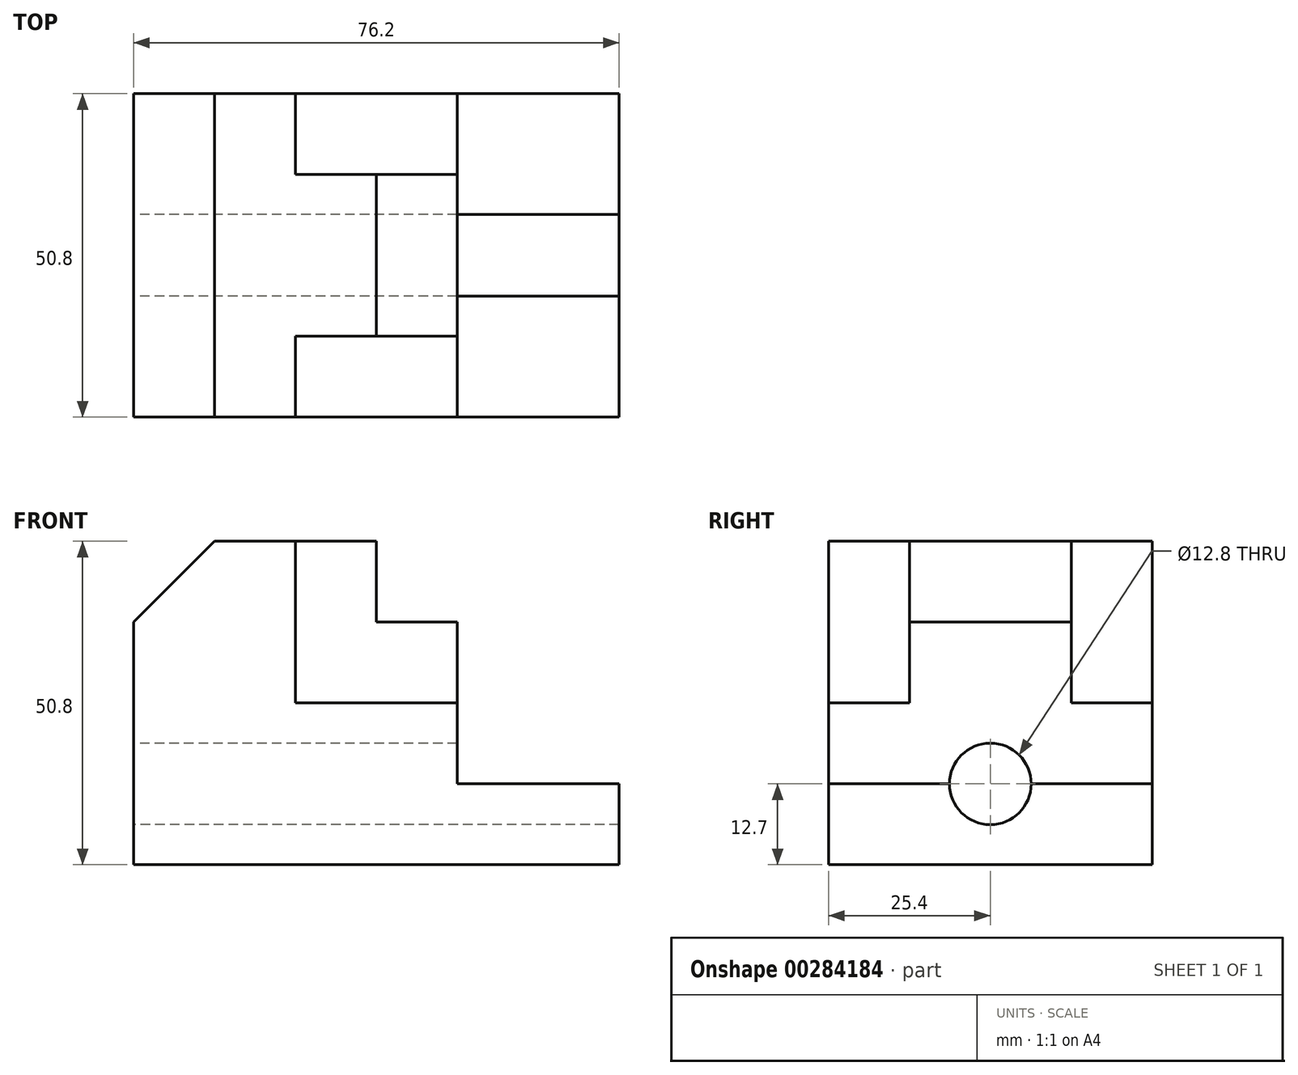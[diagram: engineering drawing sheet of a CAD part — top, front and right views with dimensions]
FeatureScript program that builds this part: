
annotation { "Feature Type Name" : "Feature", "Feature Type Description" : "" }
export const myFeature = defineFeature(function(context is Context, id is Id, definition is map)
    precondition{}
    {
        {
            var Q0;
            Q0=qCreatedBy(makeId("Front.planeOp"),FACE);
            var sketch = newSketch(context, id + "F0", { "sketchPlane" : qUnion([Q0])});
            skLineSegment(sketch, "E0", {"start": v(0, 0) * mm, "end": v(76.2, 0) * mm});
            skLineSegment(sketch, "E1", {"start": v(76.2, 0) * mm, "end": v(76.2, 12.7) * mm});
            skLineSegment(sketch, "E2", {"start": v(76.2, 12.7) * mm, "end": v(50.8, 12.7) * mm});
            skLineSegment(sketch, "E3", {"start": v(50.8, 12.7) * mm, "end": v(50.8, 38.1) * mm});
            skLineSegment(sketch, "E4", {"start": v(50.8, 38.1) * mm, "end": v(38.1, 38.1) * mm});
            skLineSegment(sketch, "E5", {"start": v(38.1, 38.1) * mm, "end": v(38.1, 50.8) * mm});
            skLineSegment(sketch, "E6", {"start": v(38.1, 50.8) * mm, "end": v(12.7, 50.8) * mm});
            skLineSegment(sketch, "E7", {"start": v(12.7, 50.8) * mm, "end": v(0, 38.1) * mm});
            skLineSegment(sketch, "E8", {"start": v(0, 38.1) * mm, "end": v(0, 0) * mm});
            skSolve(sketch);
        }
        {
            var Q0;
            Q0=makeQuery(id+"F0.imprint","IMPRINT",FACE,{"disambiguationData":[TD([[makeQuery(id+"F0.imprint","IMPRINT",EDGE,{"derivedFrom":sQuery(id+"F0.wireOp",EDGE,"E0")}),1.0]])]});
            extrude(context, id + "F1", {"entities" : qUnion([Q0]), "depth" : 50.8 * mm, "symmetric" : true});
        }
        {
            var Q0;
            Q0=makeQuery(id+"F1.opExtrude","CAP_FACE",FACE,{"disambiguationData":[OSD([sQuery(id+"F0.wireOp",EDGE,"E0"),sQuery(id+"F0.wireOp",EDGE,"E1"),sQuery(id+"F0.wireOp",EDGE,"E2"),sQuery(id+"F0.wireOp",EDGE,"E3"),sQuery(id+"F0.wireOp",EDGE,"E4"),sQuery(id+"F0.wireOp",EDGE,"E5"),sQuery(id+"F0.wireOp",EDGE,"E6"),sQuery(id+"F0.wireOp",EDGE,"E7"),sQuery(id+"F0.wireOp",EDGE,"E8")])],"isStart":false});
            var sketch = newSketch(context, id + "F2", { "sketchPlane" : qUnion([Q0])});
            skLineSegment(sketch, "E9", {"start": v(50.8, 25.4) * mm, "end": v(25.4, 25.4) * mm});
            skLineSegment(sketch, "E10", {"start": v(25.4, 25.4) * mm, "end": v(25.4, 50.8) * mm});
            skSolve(sketch);
        }
        {
            var Q0;
            {var subQ3=sQuery(id+"F2.wireOp",EDGE,"E9");Q0=makeQuery(id+"F2.imprint","IMPRINT",FACE,{"disambiguationData":[TD([[makeQuery(id+"F2.imprint","IMPRINT",EDGE,{"derivedFrom":subQ3}),-1.0]])]});}
            extrude(context, id + "F3", {"entities" : qUnion([Q0]), "operationType" : NewBodyOperationType.REMOVE, "oppositeDirection" : true, "depth" : 12.7 * mm});
        }
        {
            var Q0;
            Q0=makeQuery(id+"F1.opExtrude","CAP_FACE",FACE,{"disambiguationData":[OSD([sQuery(id+"F0.wireOp",EDGE,"E0"),sQuery(id+"F0.wireOp",EDGE,"E1"),sQuery(id+"F0.wireOp",EDGE,"E2"),sQuery(id+"F0.wireOp",EDGE,"E3"),sQuery(id+"F0.wireOp",EDGE,"E4"),sQuery(id+"F0.wireOp",EDGE,"E5"),sQuery(id+"F0.wireOp",EDGE,"E6"),sQuery(id+"F0.wireOp",EDGE,"E7"),sQuery(id+"F0.wireOp",EDGE,"E8")])],"isStart":true});
            var sketch = newSketch(context, id + "F4", { "sketchPlane" : qUnion([Q0])});
            skLineSegment(sketch, "E11", {"start": v(-50.8, 25.4) * mm, "end": v(-25.4, 25.4) * mm});
            skLineSegment(sketch, "E12", {"start": v(-25.4, 25.4) * mm, "end": v(-25.4, 50.8) * mm});
            skSolve(sketch);
        }
        {
            var Q0;
            {var subQ3=sQuery(id+"F4.wireOp",EDGE,"E11");Q0=makeQuery(id+"F4.imprint","IMPRINT",FACE,{"disambiguationData":[TD([[makeQuery(id+"F4.imprint","IMPRINT",EDGE,{"derivedFrom":subQ3}),1.0]])]});}
            extrude(context, id + "F5", {"entities" : qUnion([Q0]), "operationType" : NewBodyOperationType.REMOVE, "oppositeDirection" : true, "depth" : 12.7 * mm});
        }
        {
            var Q0;
            Q0=qCreatedBy(makeId("Right.planeOp"),FACE);
            var sketch = newSketch(context, id + "F6", { "sketchPlane" : qUnion([Q0])});
            skCircle(sketch, "E13", {"center": v(0, 12.7) * mm, "radius": 6.4 * mm});
            skSolve(sketch);
        }
        {
            var Q0;
            Q0=makeQuery(id+"F6.imprint","IMPRINT",FACE,{"disambiguationData":[TD([[makeQuery(id+"F6.imprint","IMPRINT",EDGE,{"derivedFrom":sQuery(id+"F6.wireOp",EDGE,"E13")}),1.0]])]});
            extrude(context, id + "F7", {"entities" : qUnion([Q0]), "operationType" : NewBodyOperationType.REMOVE, "endBound" : BoundingType.THROUGH_ALL, "depth" : 25.4 * mm});
        }
    });
